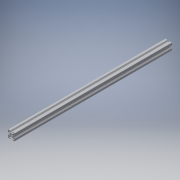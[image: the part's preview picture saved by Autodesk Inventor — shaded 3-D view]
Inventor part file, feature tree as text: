
AUTODESK INVENTOR PART (.ipt)
format: ipt  version: 2016 (Build 200138000, 138)  size: 414,720 bytes
history: native  units: in
note: dims shown in document units (in); Inventor stores cm internally (conversion verified against a paired STEP export)
features: other x3, sketch x2, extrude x1, hole x1, mirror x1
ambient origin geometry x8: Origin, YZ Plane, XZ Plane, XY Plane, X Axis, Y Axis, Z Axis, Center Point
bodies: Solid1 (feature_tree)
feature tree (8):
  other  "Blocks"
  extrude  "Extrusion1"  Depth=2.0in
  hole  "Hole1"  [1 undecoded]
  mirror  "Mirror1"
  sketch  "Sketch1"  dims[d1=0.0in d5=2.0in]
  other  "20x20"
  sketch  "Sketch3"  dims[d6=0.187in d7=0.75in d8=0.375in d9=0.25in d10=0.5635in d11=1.0in d12=0.8108in d13=1.0in d14=1.0in]
  other  "20x20:1"
note: 1 required parameter value undecoded (feature->parameter linkage not recoverable at this tier; creation-order binding heuristic only, values carry confidence <= 0.55)
